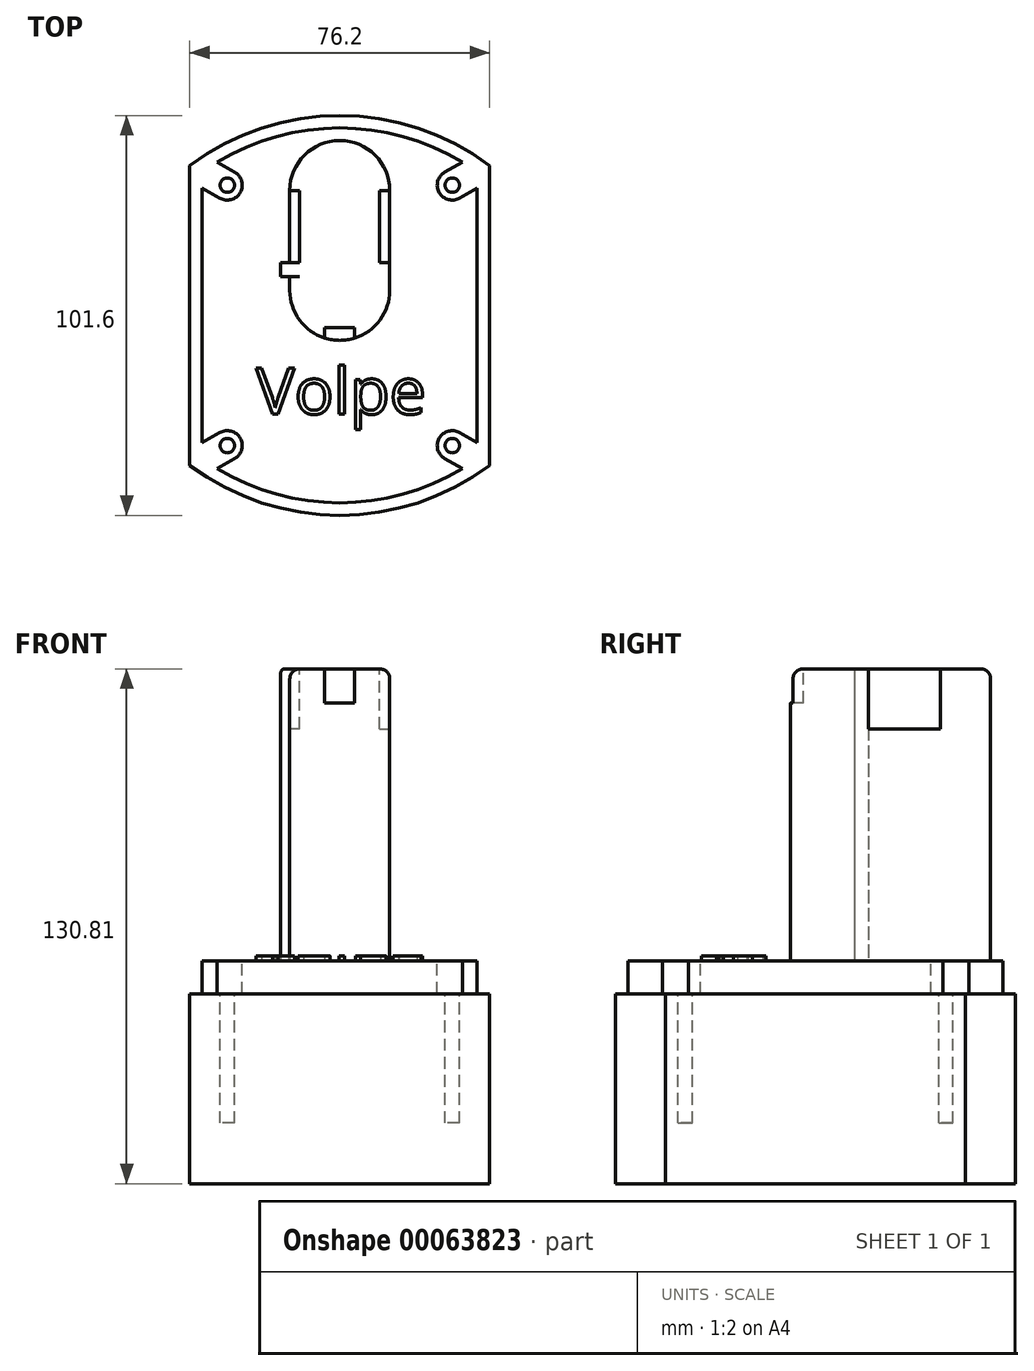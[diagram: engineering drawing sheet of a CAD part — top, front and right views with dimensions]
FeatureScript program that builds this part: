
annotation { "Feature Type Name" : "Feature", "Feature Type Description" : "" }
export const myFeature = defineFeature(function(context is Context, id is Id, definition is map)
    precondition{}
    {
        {
            var Q0;
            Q0=qCreatedBy(makeId("Top.planeOp"),FACE);
            var sketch = newSketch(context, id + "F0", { "sketchPlane" : qUnion([Q0])});
            skLineSegment(sketch, "E0.rect.bottom", {"start": v(-38.1, 38.1) * mm, "end": v(38.1, 38.1) * mm, "construction": true});
            skLineSegment(sketch, "E0.rect.top", {"start": v(-38.1, -38.1) * mm, "end": v(38.1, -38.1) * mm, "construction": true});
            skLineSegment(sketch, "E0.rect.left", {"start": v(-38.1, 38.1) * mm, "end": v(-38.1, -38.1) * mm});
            skLineSegment(sketch, "E0.rect.right", {"start": v(38.1, 38.1) * mm, "end": v(38.1, -38.1) * mm});
            skPoint(sketch, "E0.rect.middle", {"position": v(0, 0) * mm});
            skLineSegment(sketch, "E1", {"start": v(-38.1, 0) * mm, "end": v(38.1, 0) * mm, "construction": true});
            skLineSegment(sketch, "E2", {"start": v(0, 38.1) * mm, "end": v(0, 50.8) * mm, "construction": true});
            skPoint(sketch, "E2.endSnap0", {"position": v(0, 38.1) * mm});
            skArc(sketch, "E3", {"start": v(38.1, 38.1) * mm, "mid": v(0, 50.8) * mm, "end": v(-38.1, 38.1) * mm});
            skArc(sketch, "E4.MirrorCS", {"start": v(38.1, -38.1) * mm, "mid": v(0, -50.8) * mm, "end": v(-38.1, -38.1) * mm});
            skSolve(sketch);
        }
        {
            var Q0;
            Q0 = qSketchRegion(id + "F0", true);
            extrude(context, id + "F1", {"entities" : qUnion([Q0]), "oppositeDirection" : true, "depth" : 48.26 * mm});
        }
        {
            var Q0;
            Q0=qCreatedBy(makeId("Top.planeOp"),FACE);
            var sketch = newSketch(context, id + "F2", { "sketchPlane" : qUnion([Q0])});
            skArc(sketch, "E5.0", {"start": v(34.93, 36.49) * mm, "mid": v(0, 47.63) * mm, "end": v(-34.93, 36.49) * mm});
            skLineSegment(sketch, "E5.1", {"start": v(34.93, 36.49) * mm, "end": v(34.93, -36.49) * mm});
            skArc(sketch, "E5.2", {"start": v(34.93, -36.49) * mm, "mid": v(0, -47.62) * mm, "end": v(-34.93, -36.49) * mm});
            skLineSegment(sketch, "E5.3", {"start": v(-34.93, 36.49) * mm, "end": v(-34.93, -36.49) * mm});
            skSolve(sketch);
        }
        {
            var Q0;
            Q0=makeQuery(id+"F2.imprint","IMPRINT",FACE,{"disambiguationData":[TD([[makeQuery(id+"F2.imprint","IMPRINT",EDGE,{"derivedFrom":sQuery(id+"F2.wireOp",EDGE,"E5.0")}),1.0]])]});
            extrude(context, id + "F3", {"entities" : qUnion([Q0]), "operationType" : NewBodyOperationType.ADD, "depth" : 8.38 * mm});
        }
        {
            var Q0;
            Q0=makeQuery(id+"F3.opExtrude","CAP_FACE",FACE,{"disambiguationData":[OSD([sQuery(id+"F2.wireOp",EDGE,"E5.0"),sQuery(id+"F2.wireOp",EDGE,"E5.1"),sQuery(id+"F2.wireOp",EDGE,"E5.2"),sQuery(id+"F2.wireOp",EDGE,"E5.3")])],"isStart":false});
            var sketch = newSketch(context, id + "F4", { "sketchPlane" : qUnion([Q0])});
            skLineSegment(sketch, "E6.rect.bottom", {"start": v(-28.58, 33.1) * mm, "end": v(28.58, 33.1) * mm, "construction": true});
            skLineSegment(sketch, "E6.rect.top", {"start": v(-28.58, -33.1) * mm, "end": v(28.57, -33.1) * mm, "construction": true});
            skLineSegment(sketch, "E6.rect.left", {"start": v(-28.58, 33.1) * mm, "end": v(-28.58, -33.1) * mm, "construction": true});
            skLineSegment(sketch, "E6.rect.right", {"start": v(28.58, 33.1) * mm, "end": v(28.57, -33.1) * mm, "construction": true});
            skPoint(sketch, "E6.rect.middle", {"position": v(0, 0) * mm});
            skLineSegment(sketch, "E7", {"start": v(-28.58, -33.1) * mm, "end": v(-50.57, -45.8) * mm, "construction": true});
            skArc(sketch, "E8.0.startCap", {"start": v(-30.48, -29.8) * mm, "mid": v(-25.28, -31.2) * mm, "end": v(-26.67, -36.4) * mm});
            skArc(sketch, "E8.0.endCap", {"start": v(-48.67, -49.1) * mm, "mid": v(-53.87, -47.7) * mm, "end": v(-52.48, -42.5) * mm});
            skLineSegment(sketch, "E8.0.left", {"start": v(-26.67, -36.4) * mm, "end": v(-48.67, -49.1) * mm});
            skLineSegment(sketch, "E8.0.right", {"start": v(-30.48, -29.8) * mm, "end": v(-52.48, -42.5) * mm});
            skLineSegment(sketch, "E9", {"start": v(-28.58, 0) * mm, "end": v(28.58, 0) * mm, "construction": true});
            skLineSegment(sketch, "E10", {"start": v(0, 33.1) * mm, "end": v(0, -33.1) * mm, "construction": true});
            skLineSegment(sketch, "E11.MirrorCS", {"start": v(26.67, -36.4) * mm, "end": v(48.67, -49.1) * mm});
            skArc(sketch, "E12.MirrorCS", {"start": v(30.48, -29.8) * mm, "mid": v(25.28, -31.2) * mm, "end": v(26.67, -36.4) * mm});
            skLineSegment(sketch, "E13.MirrorCS", {"start": v(30.48, -29.8) * mm, "end": v(52.48, -42.5) * mm});
            skArc(sketch, "E14.MirrorCS", {"start": v(48.67, -49.1) * mm, "mid": v(53.87, -47.7) * mm, "end": v(52.48, -42.5) * mm});
            skArc(sketch, "E15.MirrorCS", {"start": v(-30.48, 29.8) * mm, "mid": v(-25.28, 31.2) * mm, "end": v(-26.67, 36.4) * mm});
            skLineSegment(sketch, "E16.MirrorCS", {"start": v(-30.48, 29.8) * mm, "end": v(-52.48, 42.5) * mm});
            skLineSegment(sketch, "E17.MirrorCS", {"start": v(-26.67, 36.4) * mm, "end": v(-48.67, 49.1) * mm});
            skArc(sketch, "E18.MirrorCS", {"start": v(-48.67, 49.1) * mm, "mid": v(-53.87, 47.7) * mm, "end": v(-52.48, 42.5) * mm});
            skLineSegment(sketch, "E19.MirrorCS", {"start": v(26.67, 36.4) * mm, "end": v(48.67, 49.1) * mm});
            skLineSegment(sketch, "E20.MirrorCS", {"start": v(30.48, 29.8) * mm, "end": v(52.48, 42.5) * mm});
            skArc(sketch, "E21.MirrorCS", {"start": v(30.48, 29.8) * mm, "mid": v(25.28, 31.2) * mm, "end": v(26.67, 36.4) * mm});
            skArc(sketch, "E22.MirrorCS", {"start": v(48.67, 49.1) * mm, "mid": v(53.87, 47.7) * mm, "end": v(52.48, 42.5) * mm});
            skCircle(sketch, "E23", {"center": v(-28.58, 33.1) * mm, "radius": 1.83 * mm, "construction": true});
            skCircle(sketch, "E24", {"center": v(28.57, -33.1) * mm, "radius": 1.83 * mm, "construction": true});
            skCircle(sketch, "E25", {"center": v(-28.58, -33.1) * mm, "radius": 1.83 * mm, "construction": true});
            skCircle(sketch, "E26", {"center": v(28.58, 33.1) * mm, "radius": 1.83 * mm, "construction": true});
            skSolve(sketch);
        }
        {
            var Q0;
            Q0 = qSketchRegion(id + "F4", true);
            var Q1;
            Q1=makeQuery(id+"F1.opExtrude","CAP_FACE",FACE,{"disambiguationData":[OSD([sQuery(id+"F0.wireOp",EDGE,"E0.rect.left"),sQuery(id+"F0.wireOp",EDGE,"E0.rect.right"),sQuery(id+"F0.wireOp",EDGE,"E3"),sQuery(id+"F0.wireOp",EDGE,"E4.MirrorCS")])],"isStart":true});
            extrude(context, id + "F5", {"entities" : qUnion([Q0]), "operationType" : NewBodyOperationType.REMOVE, "endBound" : BoundingType.UP_TO_SURFACE, "oppositeDirection" : true, "endBoundEntityFace" : qUnion([Q1]), "depth" : 25.4 * mm});
        }
        {
            var Q0;
            Q0=makeQuery(id+"F5.boolean.opBoolean","MERGE",FACE,{"derivedFrom":[makeQuery(id+"F1.opExtrude","CAP_FACE",FACE,{"disambiguationData":[OSD([sQuery(id+"F0.wireOp",EDGE,"E0.rect.left"),sQuery(id+"F0.wireOp",EDGE,"E0.rect.right"),sQuery(id+"F0.wireOp",EDGE,"E3"),sQuery(id+"F0.wireOp",EDGE,"E4.MirrorCS")])],"isStart":true})],"fromTools":[makeQuery(id+"F5.opExtrude","CAP_FACE",FACE,{"disambiguationData":[OSD([sQuery(id+"F4.wireOp",EDGE,"E8.0.startCap"),sQuery(id+"F4.wireOp",EDGE,"E8.0.endCap"),sQuery(id+"F4.wireOp",EDGE,"E8.0.left"),sQuery(id+"F4.wireOp",EDGE,"E8.0.right")])],"isStart":false}),makeQuery(id+"F5.opExtrude","CAP_FACE",FACE,{"disambiguationData":[OSD([sQuery(id+"F4.wireOp",EDGE,"E11.MirrorCS"),sQuery(id+"F4.wireOp",EDGE,"E12.MirrorCS"),sQuery(id+"F4.wireOp",EDGE,"E13.MirrorCS"),sQuery(id+"F4.wireOp",EDGE,"E14.MirrorCS")])],"isStart":false}),makeQuery(id+"F5.opExtrude","CAP_FACE",FACE,{"disambiguationData":[OSD([sQuery(id+"F4.wireOp",EDGE,"E15.MirrorCS"),sQuery(id+"F4.wireOp",EDGE,"E16.MirrorCS"),sQuery(id+"F4.wireOp",EDGE,"E17.MirrorCS"),sQuery(id+"F4.wireOp",EDGE,"E18.MirrorCS")])],"isStart":false}),makeQuery(id+"F5.opExtrude","CAP_FACE",FACE,{"disambiguationData":[OSD([sQuery(id+"F4.wireOp",EDGE,"E19.MirrorCS"),sQuery(id+"F4.wireOp",EDGE,"E20.MirrorCS"),sQuery(id+"F4.wireOp",EDGE,"E21.MirrorCS"),sQuery(id+"F4.wireOp",EDGE,"E22.MirrorCS")])],"isStart":false})]});
            var sketch = newSketch(context, id + "F6", { "sketchPlane" : qUnion([Q0])});
            skCircle(sketch, "E27.0", {"center": v(-28.58, 33.1) * mm, "radius": 1.83 * mm});
            skCircle(sketch, "E27.1", {"center": v(28.58, 33.1) * mm, "radius": 1.83 * mm});
            skCircle(sketch, "E27.2", {"center": v(28.57, -33.1) * mm, "radius": 1.83 * mm});
            skCircle(sketch, "E27.3", {"center": v(-28.58, -33.1) * mm, "radius": 1.83 * mm});
            skSolve(sketch);
        }
        {
            var Q0;
            Q0 = qSketchRegion(id + "F6", true);
            extrude(context, id + "F7", {"entities" : qUnion([Q0]), "operationType" : NewBodyOperationType.REMOVE, "oppositeDirection" : true, "depth" : 32.84 * mm});
        }
        {
            var Q0;
            Q0=qCreatedBy(makeId("Top.planeOp"),FACE);
            var sketch = newSketch(context, id + "F8", { "sketchPlane" : qUnion([Q0])});
            skLineSegment(sketch, "E28", {"start": v(0, 6.35) * mm, "end": v(0, 31.75) * mm, "construction": true});
            skArc(sketch, "E29.0.startCap", {"start": v(12.7, 6.35) * mm, "mid": v(0, -6.35) * mm, "end": v(-12.7, 6.35) * mm});
            skArc(sketch, "E29.0.endCap", {"start": v(-12.7, 31.75) * mm, "mid": v(0, 44.45) * mm, "end": v(12.7, 31.75) * mm});
            skLineSegment(sketch, "E29.0.left", {"start": v(-12.7, 6.35) * mm, "end": v(-12.7, 31.75) * mm});
            skLineSegment(sketch, "E29.0.right", {"start": v(12.7, 6.35) * mm, "end": v(12.7, 31.75) * mm});
            skLineSegment(sketch, "E30", {"start": v(0, 0) * mm, "end": v(0, 19.05) * mm, "construction": true});
            skSolve(sketch);
        }
        {
            var Q0;
            Q0 = qSketchRegion(id + "F8", true);
            extrude(context, id + "F9", {"entities" : qUnion([Q0]), "operationType" : NewBodyOperationType.ADD, "depth" : 82.55 * mm});
        }
        {
            var Q0;
            Q0=makeQuery(id+"F3.opExtrude","CAP_FACE",FACE,{"disambiguationData":[OSD([sQuery(id+"F2.wireOp",EDGE,"E5.0"),sQuery(id+"F2.wireOp",EDGE,"E5.1"),sQuery(id+"F2.wireOp",EDGE,"E5.2"),sQuery(id+"F2.wireOp",EDGE,"E5.3")])],"isStart":false});
            var sketch = newSketch(context, id + "F10", { "sketchPlane" : qUnion([Q0])});
            skLineSegment(sketch, "E31.bottom", {"start": v(-12.7, 13.46) * mm, "end": v(-14.99, 13.46) * mm});
            skLineSegment(sketch, "E31.top", {"start": v(-12.7, 9.9) * mm, "end": v(-14.99, 9.9) * mm});
            skLineSegment(sketch, "E31.left", {"start": v(-12.7, 13.46) * mm, "end": v(-12.7, 9.9) * mm});
            skLineSegment(sketch, "E31.right", {"start": v(-14.99, 13.46) * mm, "end": v(-14.99, 9.9) * mm});
            skSolve(sketch);
        }
        {
            var Q0;
            Q0 = qSketchRegion(id + "F10", true);
            var Q1;
            Q1=makeQuery(id+"F9.opExtrude","CAP_FACE",FACE,{"disambiguationData":[OSD([sQuery(id+"F8.wireOp",EDGE,"E29.0.startCap"),sQuery(id+"F8.wireOp",EDGE,"E29.0.endCap"),sQuery(id+"F8.wireOp",EDGE,"E29.0.left"),sQuery(id+"F8.wireOp",EDGE,"E29.0.right")])],"isStart":false});
            extrude(context, id + "F11", {"entities" : qUnion([Q0]), "operationType" : NewBodyOperationType.ADD, "endBound" : BoundingType.UP_TO_SURFACE, "endBoundEntityFace" : qUnion([Q1]), "depth" : 25.4 * mm});
        }
        {
            var Q0;
            Q0=makeQuery(id+"F9.opExtrude","CAP_EDGE",EDGE,{"disambiguationData":[OSD([sQuery(id+"F8.wireOp",EDGE,"E29.0.right")])],"isStart":false});
            fillet(context, id + "F12", {"entities" : qUnion([Q0]), "radius" : 2.54 * mm, "tangentPropagation" : true, "allowEdgeOverflow" : false});
        }
        {
            var Q0;
            Q0=makeQuery(id+"F11.boolean.opBoolean","MERGE",FACE,{"derivedFrom":[makeQuery(id+"F9.opExtrude","CAP_FACE",FACE,{"disambiguationData":[OSD([sQuery(id+"F8.wireOp",EDGE,"E29.0.startCap"),sQuery(id+"F8.wireOp",EDGE,"E29.0.endCap"),sQuery(id+"F8.wireOp",EDGE,"E29.0.left"),sQuery(id+"F8.wireOp",EDGE,"E29.0.right")])],"isStart":false}),makeQuery(id+"F11.opExtrude","CAP_FACE",FACE,{"disambiguationData":[OSD([sQuery(id+"F10.wireOp",EDGE,"E31.bottom"),sQuery(id+"F10.wireOp",EDGE,"E31.top"),sQuery(id+"F10.wireOp",EDGE,"E31.left"),sQuery(id+"F10.wireOp",EDGE,"E31.right")])],"isStart":false})]});
            var sketch = newSketch(context, id + "F13", { "sketchPlane" : qUnion([Q0])});
            skLineSegment(sketch, "E32.bottom", {"start": v(10.16, 31.75) * mm, "end": v(12.7, 31.75) * mm});
            skLineSegment(sketch, "E32.top", {"start": v(10.16, 13.46) * mm, "end": v(12.7, 13.46) * mm});
            skLineSegment(sketch, "E32.left", {"start": v(10.16, 31.75) * mm, "end": v(10.16, 13.46) * mm});
            skLineSegment(sketch, "E32.right", {"start": v(12.7, 31.75) * mm, "end": v(12.7, 13.46) * mm});
            skLineSegment(sketch, "E33.MirrorCS", {"start": v(-10.16, 31.75) * mm, "end": v(-10.16, 13.46) * mm});
            skLineSegment(sketch, "E34.MirrorCS", {"start": v(-10.16, 31.75) * mm, "end": v(-12.7, 31.75) * mm});
            skLineSegment(sketch, "E35.MirrorCS", {"start": v(-12.7, 31.75) * mm, "end": v(-12.7, 13.46) * mm});
            skLineSegment(sketch, "E36.MirrorCS", {"start": v(-10.16, 13.46) * mm, "end": v(-12.7, 13.46) * mm});
            skArc(sketch, "E37.0", {"start": v(3.81, -5.77) * mm, "mid": v(0, -6.35) * mm, "end": v(-3.8, -5.77) * mm, "construction": true});
            skArc(sketch, "E37.1", {"start": v(-10.16, 6.35) * mm, "mid": v(0, -3.81) * mm, "end": v(10.16, 6.35) * mm, "construction": true});
            skLineSegment(sketch, "E38", {"start": v(-3.81, -5.77) * mm, "end": v(-3.81, -3.07) * mm, "construction": true});
            skLineSegment(sketch, "E39", {"start": v(-3.81, -3.07) * mm, "end": v(3.81, -3.07) * mm, "construction": true});
            skLineSegment(sketch, "E40", {"start": v(3.81, -3.07) * mm, "end": v(3.81, -5.77) * mm, "construction": true});
            skPoint(sketch, "E41.orphan", {"position": v(-12.7, 6.35) * mm});
            skPoint(sketch, "E42.orphan", {"position": v(12.7, 6.35) * mm});
            skSolve(sketch);
        }
        {
            var Q0;
            Q0 = qSketchRegion(id + "F13", true);
            extrude(context, id + "F14", {"entities" : qUnion([Q0]), "operationType" : NewBodyOperationType.REMOVE, "oppositeDirection" : true, "depth" : 15.24 * mm});
        }
        {
            var Q0;
            {var subQ5=sQuery(id+"F13.wireOp",EDGE,"E32.left");Q0=makeQuery(id+"F13.imprint","IMPRINT",FACE,{"disambiguationData":[TD([[makeQuery(id+"F13.imprint","IMPRINT",EDGE,{"derivedFrom":subQ5}),1.0]])]});}
            var sketch = newSketch(context, id + "F15", { "sketchPlane" : qUnion([Q0])});
            skLineSegment(sketch, "E43.0", {"start": v(-3.81, -3.07) * mm, "end": v(3.81, -3.07) * mm});
            skLineSegment(sketch, "E43.1", {"start": v(3.81, -3.07) * mm, "end": v(3.81, -5.77) * mm});
            skLineSegment(sketch, "E43.2", {"start": v(-3.81, -5.77) * mm, "end": v(-3.81, -3.07) * mm});
            skArc(sketch, "E44.0", {"start": v(3.8, -5.77) * mm, "mid": v(0, -6.35) * mm, "end": v(-3.81, -5.77) * mm});
            skPoint(sketch, "E45.orphan", {"position": v(-12.7, 6.35) * mm});
            skPoint(sketch, "E46.orphan", {"position": v(12.7, 6.35) * mm});
            skSolve(sketch);
        }
        {
            var Q0;
            Q0 = qSketchRegion(id + "F15", true);
            extrude(context, id + "F16", {"entities" : qUnion([Q0]), "operationType" : NewBodyOperationType.REMOVE, "oppositeDirection" : true, "depth" : 8.64 * mm});
        }
        {
            var Q0;
            Q0=makeQuery(id+"F11.opExtrude","CAP_EDGE",EDGE,{"disambiguationData":[OSD([sQuery(id+"F10.wireOp",EDGE,"E31.right")])],"isStart":false});
            fillet(context, id + "F17", {"entities" : qUnion([Q0]), "radius" : 1.02 * mm, "tangentPropagation" : true, "allowEdgeOverflow" : false});
        }
        {
            var Q0;
            Q0=makeQuery(id+"F3.opExtrude","CAP_FACE",FACE,{"disambiguationData":[OSD([sQuery(id+"F2.wireOp",EDGE,"E5.0"),sQuery(id+"F2.wireOp",EDGE,"E5.1"),sQuery(id+"F2.wireOp",EDGE,"E5.2"),sQuery(id+"F2.wireOp",EDGE,"E5.3")])],"isStart":false});
            var sketch = newSketch(context, id + "F18", { "sketchPlane" : qUnion([Q0])});
            skText(sketch, "E47", { "text": "Volpe", "fontName": "OpenSans-Regular.ttf"});
            const initialGuessF18  = {"E47": [-0.02127, -0.02507, 1, 0, 0.01183]};
            skSetInitialGuess(sketch, initialGuessF18);
            skSolve(sketch);
        }
        {
            var Q0;
            Q0 = qSketchRegion(id + "F18", true);
            extrude(context, id + "F19", {"entities" : qUnion([Q0]), "operationType" : NewBodyOperationType.ADD, "depth" : 1.27 * mm});
        }
    });
